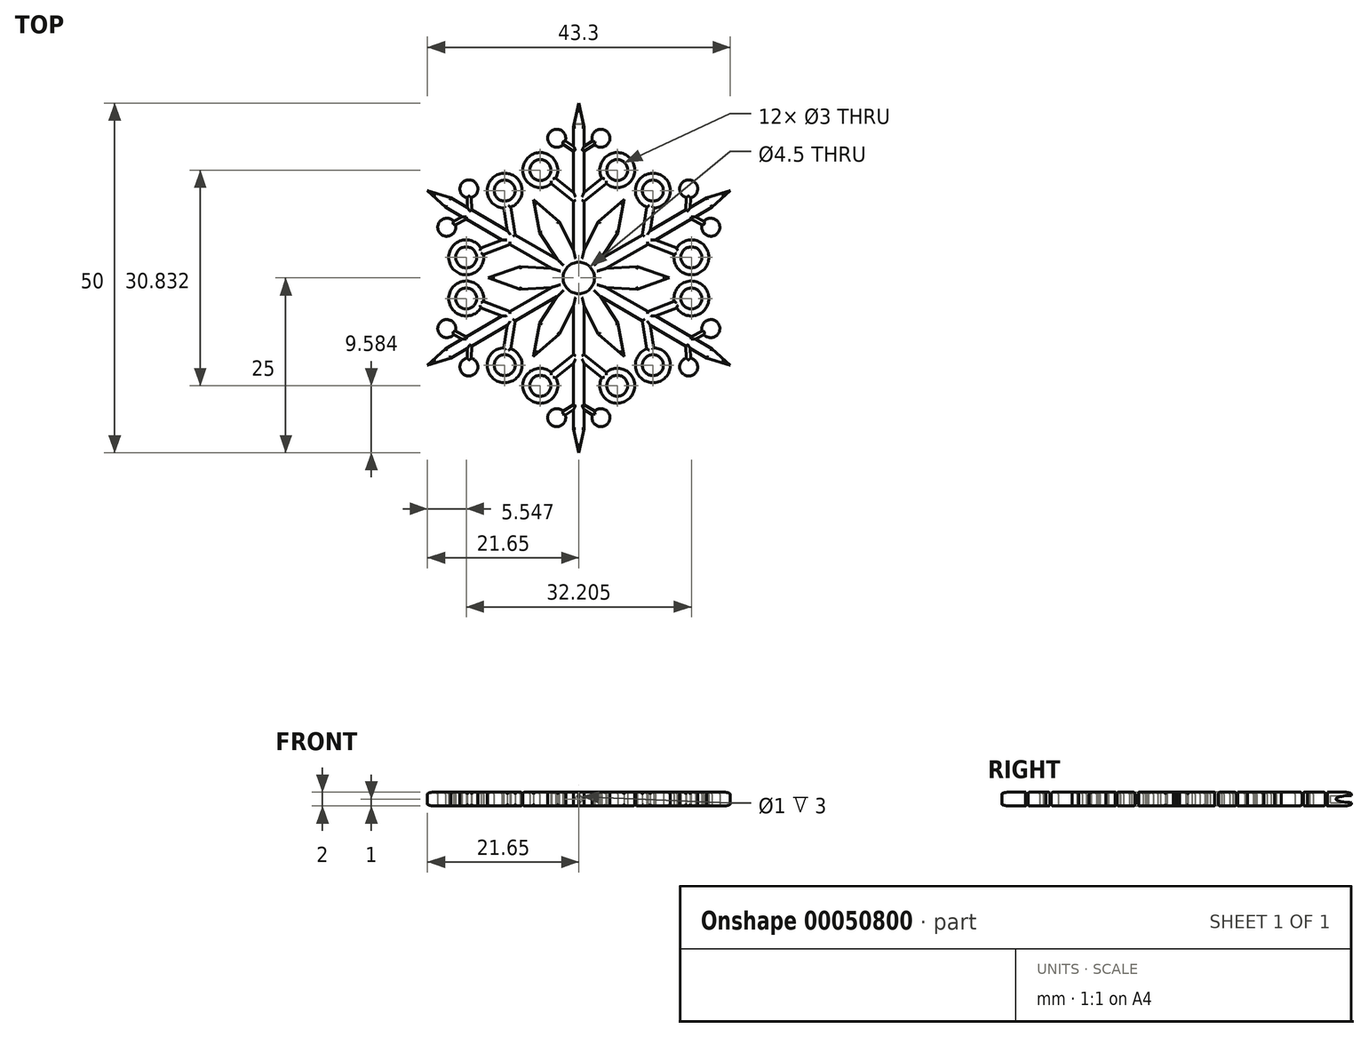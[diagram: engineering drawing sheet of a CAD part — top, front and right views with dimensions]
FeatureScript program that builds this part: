
annotation { "Feature Type Name" : "Feature", "Feature Type Description" : "" }
export const myFeature = defineFeature(function(context is Context, id is Id, definition is map)
    precondition{}
    {
        {
            var Q0;
            Q0=qCreatedBy(makeId("Top.planeOp"),FACE);
            var sketch = newSketch(context, id + "F0", { "sketchPlane" : qUnion([Q0])});
            skCircle(sketch, "E0", {"center": v(0, 0) * mm, "radius": 25 * mm, "construction": true});
            skLineSegment(sketch, "E1", {"start": v(0, 0) * mm, "end": v(0, 37.67) * mm, "construction": true});
            skLineSegment(sketch, "E2", {"start": v(0, 0) * mm, "end": v(12.93, 22.4) * mm, "construction": true});
            skLineSegment(sketch, "E3", {"start": v(0, 0) * mm, "end": v(-17.9, 31.01) * mm, "construction": true});
            skLineSegment(sketch, "E4", {"start": v(0, 25) * mm, "end": v(0.77, 21.58) * mm});
            skLineSegment(sketch, "E5", {"start": v(0.77, 21.58) * mm, "end": v(0.77, 18.84) * mm});
            skPoint(sketch, "E5.endSnap0", {"position": v(0, 18.84) * mm});
            skLineSegment(sketch, "E6", {"start": v(0.77, 18.84) * mm, "end": v(1.94, 19.56) * mm});
            skLineSegment(sketch, "E7", {"start": v(2.26, 19.06) * mm, "end": v(0.77, 18.13) * mm});
            skLineSegment(sketch, "E8", {"start": v(0.77, 18.13) * mm, "end": v(0.77, 12.24) * mm});
            skLineSegment(sketch, "E9", {"start": v(0.77, 12.24) * mm, "end": v(3.28, 14.27) * mm});
            skLineSegment(sketch, "E10", {"start": v(3.91, 13.49) * mm, "end": v(0.77, 10.95) * mm});
            skLineSegment(sketch, "E11", {"start": v(0.77, 10.95) * mm, "end": v(0.77, 4) * mm});
            skLineSegment(sketch, "E12", {"start": v(0.77, 4) * mm, "end": v(2.8, 8.06) * mm});
            skLineSegment(sketch, "E13", {"start": v(2.8, 8.06) * mm, "end": v(6.47, 11.2) * mm});
            skLineSegment(sketch, "E14", {"start": v(6.47, 11.2) * mm, "end": v(0, 0) * mm});
            skArc(sketch, "E15", {"start": v(2.26, 19.06) * mm, "mid": v(4.26, 20.65) * mm, "end": v(1.94, 19.56) * mm});
            skArc(sketch, "E16", {"start": v(3.91, 13.49) * mm, "mid": v(7.45, 16.99) * mm, "end": v(3.28, 14.27) * mm});
            skLineSegment(sketch, "E17.MirrorCS", {"start": v(-2.26, 19.06) * mm, "end": v(-0.77, 18.13) * mm});
            skLineSegment(sketch, "E18.MirrorCS", {"start": v(-0.77, 18.84) * mm, "end": v(-1.94, 19.56) * mm});
            skLineSegment(sketch, "E19.MirrorCS", {"start": v(-0.77, 10.95) * mm, "end": v(-0.77, 4) * mm});
            skArc(sketch, "E20.MirrorCS", {"start": v(-3.91, 13.49) * mm, "mid": v(-7.45, 16.99) * mm, "end": v(-3.28, 14.27) * mm});
            skLineSegment(sketch, "E21.MirrorCS", {"start": v(-6.47, 11.2) * mm, "end": v(0, 0) * mm});
            skLineSegment(sketch, "E22.MirrorCS", {"start": v(-3.91, 13.49) * mm, "end": v(-0.77, 10.95) * mm});
            skLineSegment(sketch, "E23.MirrorCS", {"start": v(-0.77, 4) * mm, "end": v(-2.8, 8.06) * mm});
            skLineSegment(sketch, "E24.MirrorCS", {"start": v(-0.77, 12.24) * mm, "end": v(-3.28, 14.27) * mm});
            skLineSegment(sketch, "E25.MirrorCS", {"start": v(-2.8, 8.06) * mm, "end": v(-6.47, 11.2) * mm});
            skLineSegment(sketch, "E26.MirrorCS", {"start": v(-0.77, 18.13) * mm, "end": v(-0.77, 12.24) * mm});
            skArc(sketch, "E27.MirrorCS", {"start": v(-2.26, 19.06) * mm, "mid": v(-4.26, 20.65) * mm, "end": v(-1.94, 19.56) * mm});
            skLineSegment(sketch, "E28.MirrorCS", {"start": v(0, 25) * mm, "end": v(-0.77, 21.58) * mm});
            skLineSegment(sketch, "E29.MirrorCS", {"start": v(-0.77, 21.58) * mm, "end": v(-0.77, 18.84) * mm});
            skLineSegment(sketch, "E30", {"start": v(1.35, 19.2) * mm, "end": v(1.67, 18.7) * mm, "construction": true});
            skLineSegment(sketch, "E31", {"start": v(1.51, 18.95) * mm, "end": v(4.75, 20.96) * mm, "construction": true});
            skLineSegment(sketch, "E32", {"start": v(2.03, 13.25) * mm, "end": v(2.65, 12.47) * mm, "construction": true});
            skLineSegment(sketch, "E33", {"start": v(2.34, 12.86) * mm, "end": v(8.1, 17.52) * mm, "construction": true});
            skCircle(sketch, "E34", {"center": v(5.5, 15.42) * mm, "radius": 1.5 * mm});
            skCircle(sketch, "E35.MirrorC", {"center": v(-5.5, 15.42) * mm, "radius": 1.5 * mm});
            skSolve(sketch);
        }
        {
            var Q0;
            Q0=makeQuery(id+"F0.imprint","IMPRINT",FACE,{"disambiguationData":[TD([[makeQuery(id+"F0.imprint","IMPRINT",EDGE,{"derivedFrom":sQuery(id+"F0.wireOp",EDGE,"E4")}),-1.0]])]});
            extrude(context, id + "F1", {"entities" : qUnion([Q0]), "endBound" : BoundingType.SYMMETRIC, "depth" : 2 * mm});
        }
        {
            var Q0;
            Q0=qCreatedBy(makeId("Front.planeOp"),FACE);
            var sketch = newSketch(context, id + "F2", { "sketchPlane" : qUnion([Q0])});
            skLineSegment(sketch, "E36", {"start": v(0, -15.67) * mm, "end": v(0, 28.6) * mm, "construction": true});
            skSolve(sketch);
        }
        {
            var Q0;
            Q0=makeQuery(id+"F1.opExtrude","SWEPT_BODY",BODY,{"disambiguationData":[OSD([sQuery(id+"F0.wireOp",EDGE,"E4"),sQuery(id+"F0.wireOp",EDGE,"E5"),sQuery(id+"F0.wireOp",EDGE,"E6"),sQuery(id+"F0.wireOp",EDGE,"E7"),sQuery(id+"F0.wireOp",EDGE,"E8"),sQuery(id+"F0.wireOp",EDGE,"E9"),sQuery(id+"F0.wireOp",EDGE,"E10"),sQuery(id+"F0.wireOp",EDGE,"E11"),sQuery(id+"F0.wireOp",EDGE,"E12"),sQuery(id+"F0.wireOp",EDGE,"E13"),sQuery(id+"F0.wireOp",EDGE,"E14"),sQuery(id+"F0.wireOp",EDGE,"E15"),sQuery(id+"F0.wireOp",EDGE,"E16"),sQuery(id+"F0.wireOp",EDGE,"E17.MirrorCS"),sQuery(id+"F0.wireOp",EDGE,"E18.MirrorCS"),sQuery(id+"F0.wireOp",EDGE,"E19.MirrorCS"),sQuery(id+"F0.wireOp",EDGE,"E20.MirrorCS"),sQuery(id+"F0.wireOp",EDGE,"E21.MirrorCS"),sQuery(id+"F0.wireOp",EDGE,"E22.MirrorCS"),sQuery(id+"F0.wireOp",EDGE,"E23.MirrorCS"),sQuery(id+"F0.wireOp",EDGE,"E24.MirrorCS"),sQuery(id+"F0.wireOp",EDGE,"E25.MirrorCS"),sQuery(id+"F0.wireOp",EDGE,"E26.MirrorCS"),sQuery(id+"F0.wireOp",EDGE,"E27.MirrorCS"),sQuery(id+"F0.wireOp",EDGE,"E28.MirrorCS"),sQuery(id+"F0.wireOp",EDGE,"E29.MirrorCS")])]});
            var Q1;
            Q1=sQuery(id+"F2.wireOp",EDGE,"E36");
            circularPattern(context, id + "F3", {"operationType" : NewBodyOperationType.ADD, "entities" : qUnion([Q0]), "axis" : qUnion([Q1]), "angle" : 360 * degree, "instanceCount" : round(6), "equalSpace" : true});
        }
        {
            var Q0;
            {var subQ0=makeQuery(id+"F1.opExtrude","CAP_FACE",FACE,{"disambiguationData":[OSD([sQuery(id+"F0.wireOp",EDGE,"E4"),sQuery(id+"F0.wireOp",EDGE,"E5"),sQuery(id+"F0.wireOp",EDGE,"E6"),sQuery(id+"F0.wireOp",EDGE,"E7"),sQuery(id+"F0.wireOp",EDGE,"E8"),sQuery(id+"F0.wireOp",EDGE,"E9"),sQuery(id+"F0.wireOp",EDGE,"E10"),sQuery(id+"F0.wireOp",EDGE,"E11"),sQuery(id+"F0.wireOp",EDGE,"E12"),sQuery(id+"F0.wireOp",EDGE,"E13"),sQuery(id+"F0.wireOp",EDGE,"E14"),sQuery(id+"F0.wireOp",EDGE,"E15"),sQuery(id+"F0.wireOp",EDGE,"E16"),sQuery(id+"F0.wireOp",EDGE,"E17.MirrorCS"),sQuery(id+"F0.wireOp",EDGE,"E18.MirrorCS"),sQuery(id+"F0.wireOp",EDGE,"E19.MirrorCS"),sQuery(id+"F0.wireOp",EDGE,"E20.MirrorCS"),sQuery(id+"F0.wireOp",EDGE,"E21.MirrorCS"),sQuery(id+"F0.wireOp",EDGE,"E22.MirrorCS"),sQuery(id+"F0.wireOp",EDGE,"E23.MirrorCS"),sQuery(id+"F0.wireOp",EDGE,"E24.MirrorCS"),sQuery(id+"F0.wireOp",EDGE,"E25.MirrorCS"),sQuery(id+"F0.wireOp",EDGE,"E26.MirrorCS"),sQuery(id+"F0.wireOp",EDGE,"E27.MirrorCS"),sQuery(id+"F0.wireOp",EDGE,"E28.MirrorCS"),sQuery(id+"F0.wireOp",EDGE,"E29.MirrorCS"),sQuery(id+"F0.wireOp",EDGE,"E34"),sQuery(id+"F0.wireOp",EDGE,"E35.MirrorC")])],"isStart":false});Q0=makeQuery(id+"F3.boolean.opBoolean","MERGE",FACE,{"derivedFrom":[subQ0,makeQuery(id+"F3.opPattern","COPY",FACE,{"derivedFrom":subQ0,"instanceName":"1"}),makeQuery(id+"F3.opPattern","COPY",FACE,{"derivedFrom":subQ0,"instanceName":"2"}),makeQuery(id+"F3.opPattern","COPY",FACE,{"derivedFrom":subQ0,"instanceName":"3"}),makeQuery(id+"F3.opPattern","COPY",FACE,{"derivedFrom":subQ0,"instanceName":"4"}),makeQuery(id+"F3.opPattern","COPY",FACE,{"derivedFrom":subQ0,"instanceName":"5"})]});}
            var sketch = newSketch(context, id + "F4", { "sketchPlane" : qUnion([Q0])});
            skCircle(sketch, "E37", {"center": v(0, 0) * mm, "radius": 2.25 * mm});
            skSolve(sketch);
        }
        {
            var Q0;
            Q0=qSketchRegion(id+"F4",true);
            extrude(context, id + "F5", {"entities" : qUnion([Q0]), "operationType" : NewBodyOperationType.REMOVE, "endBound" : BoundingType.THROUGH_ALL, "oppositeDirection" : true, "depth" : 25 * mm});
        }
        {
            var Q0;
            {var subQ0=makeQuery(id+"F1.opExtrude","CAP_FACE",FACE,{"disambiguationData":[OSD([sQuery(id+"F0.wireOp",EDGE,"E4"),sQuery(id+"F0.wireOp",EDGE,"E5"),sQuery(id+"F0.wireOp",EDGE,"E6"),sQuery(id+"F0.wireOp",EDGE,"E7"),sQuery(id+"F0.wireOp",EDGE,"E8"),sQuery(id+"F0.wireOp",EDGE,"E9"),sQuery(id+"F0.wireOp",EDGE,"E10"),sQuery(id+"F0.wireOp",EDGE,"E11"),sQuery(id+"F0.wireOp",EDGE,"E12"),sQuery(id+"F0.wireOp",EDGE,"E13"),sQuery(id+"F0.wireOp",EDGE,"E14"),sQuery(id+"F0.wireOp",EDGE,"E15"),sQuery(id+"F0.wireOp",EDGE,"E16"),sQuery(id+"F0.wireOp",EDGE,"E17.MirrorCS"),sQuery(id+"F0.wireOp",EDGE,"E18.MirrorCS"),sQuery(id+"F0.wireOp",EDGE,"E19.MirrorCS"),sQuery(id+"F0.wireOp",EDGE,"E20.MirrorCS"),sQuery(id+"F0.wireOp",EDGE,"E21.MirrorCS"),sQuery(id+"F0.wireOp",EDGE,"E22.MirrorCS"),sQuery(id+"F0.wireOp",EDGE,"E23.MirrorCS"),sQuery(id+"F0.wireOp",EDGE,"E24.MirrorCS"),sQuery(id+"F0.wireOp",EDGE,"E25.MirrorCS"),sQuery(id+"F0.wireOp",EDGE,"E26.MirrorCS"),sQuery(id+"F0.wireOp",EDGE,"E27.MirrorCS"),sQuery(id+"F0.wireOp",EDGE,"E28.MirrorCS"),sQuery(id+"F0.wireOp",EDGE,"E29.MirrorCS"),sQuery(id+"F0.wireOp",EDGE,"E34"),sQuery(id+"F0.wireOp",EDGE,"E35.MirrorC")])],"isStart":false});Q0=makeQuery(id+"F3.boolean.opBoolean","MERGE",FACE,{"derivedFrom":[subQ0,makeQuery(id+"F3.opPattern","COPY",FACE,{"derivedFrom":subQ0,"instanceName":"1"}),makeQuery(id+"F3.opPattern","COPY",FACE,{"derivedFrom":subQ0,"instanceName":"2"}),makeQuery(id+"F3.opPattern","COPY",FACE,{"derivedFrom":subQ0,"instanceName":"3"}),makeQuery(id+"F3.opPattern","COPY",FACE,{"derivedFrom":subQ0,"instanceName":"4"}),makeQuery(id+"F3.opPattern","COPY",FACE,{"derivedFrom":subQ0,"instanceName":"5"})]});}
            var Q1;
            {var subQ0=makeQuery(id+"F1.opExtrude","CAP_FACE",FACE,{"disambiguationData":[OSD([sQuery(id+"F0.wireOp",EDGE,"E4"),sQuery(id+"F0.wireOp",EDGE,"E5"),sQuery(id+"F0.wireOp",EDGE,"E6"),sQuery(id+"F0.wireOp",EDGE,"E7"),sQuery(id+"F0.wireOp",EDGE,"E8"),sQuery(id+"F0.wireOp",EDGE,"E9"),sQuery(id+"F0.wireOp",EDGE,"E10"),sQuery(id+"F0.wireOp",EDGE,"E11"),sQuery(id+"F0.wireOp",EDGE,"E12"),sQuery(id+"F0.wireOp",EDGE,"E13"),sQuery(id+"F0.wireOp",EDGE,"E14"),sQuery(id+"F0.wireOp",EDGE,"E15"),sQuery(id+"F0.wireOp",EDGE,"E16"),sQuery(id+"F0.wireOp",EDGE,"E17.MirrorCS"),sQuery(id+"F0.wireOp",EDGE,"E18.MirrorCS"),sQuery(id+"F0.wireOp",EDGE,"E19.MirrorCS"),sQuery(id+"F0.wireOp",EDGE,"E20.MirrorCS"),sQuery(id+"F0.wireOp",EDGE,"E21.MirrorCS"),sQuery(id+"F0.wireOp",EDGE,"E22.MirrorCS"),sQuery(id+"F0.wireOp",EDGE,"E23.MirrorCS"),sQuery(id+"F0.wireOp",EDGE,"E24.MirrorCS"),sQuery(id+"F0.wireOp",EDGE,"E25.MirrorCS"),sQuery(id+"F0.wireOp",EDGE,"E26.MirrorCS"),sQuery(id+"F0.wireOp",EDGE,"E27.MirrorCS"),sQuery(id+"F0.wireOp",EDGE,"E28.MirrorCS"),sQuery(id+"F0.wireOp",EDGE,"E29.MirrorCS"),sQuery(id+"F0.wireOp",EDGE,"E34"),sQuery(id+"F0.wireOp",EDGE,"E35.MirrorC")])],"isStart":true});Q1=makeQuery(id+"F3.boolean.opBoolean","MERGE",FACE,{"derivedFrom":[subQ0,makeQuery(id+"F3.opPattern","COPY",FACE,{"derivedFrom":subQ0,"instanceName":"1"}),makeQuery(id+"F3.opPattern","COPY",FACE,{"derivedFrom":subQ0,"instanceName":"2"}),makeQuery(id+"F3.opPattern","COPY",FACE,{"derivedFrom":subQ0,"instanceName":"3"}),makeQuery(id+"F3.opPattern","COPY",FACE,{"derivedFrom":subQ0,"instanceName":"4"}),makeQuery(id+"F3.opPattern","COPY",FACE,{"derivedFrom":subQ0,"instanceName":"5"})]});}
            fillet(context, id + "F6", {"entities" : qUnion([Q0, Q1]), "radius" : 0.3 * mm, "tangentPropagation" : true, "allowEdgeOverflow" : false});
        }
        {
            var Q0;
            Q0=qCreatedBy(makeId("Front.planeOp"),FACE);
            cPlane(context, id + "F7", {"entities" : qUnion([Q0]), "cplaneType" : CPlaneType.OFFSET, "offset" : 25 * mm, "oppositeDirection" : true, "width" : 150 * mm, "height" : 150 * mm});
        }
        {
            var Q0;
            Q0=qCreatedBy(id+"F7.planeOp",FACE);
            var sketch = newSketch(context, id + "F8", { "sketchPlane" : qUnion([Q0])});
            skCircle(sketch, "E38", {"center": v(0, 0) * mm, "radius": 0.5 * mm});
            skSolve(sketch);
        }
        {
            var Q0;
            Q0=makeQuery(id+"F8.imprint","IMPRINT",FACE,{"disambiguationData":[TD([[makeQuery(id+"F8.imprint","IMPRINT",EDGE,{"derivedFrom":sQuery(id+"F8.wireOp",EDGE,"E38")}),1.0]])]});
            extrude(context, id + "F9", {"entities" : qUnion([Q0]), "operationType" : NewBodyOperationType.REMOVE, "depth" : 3 * mm});
        }
    });
